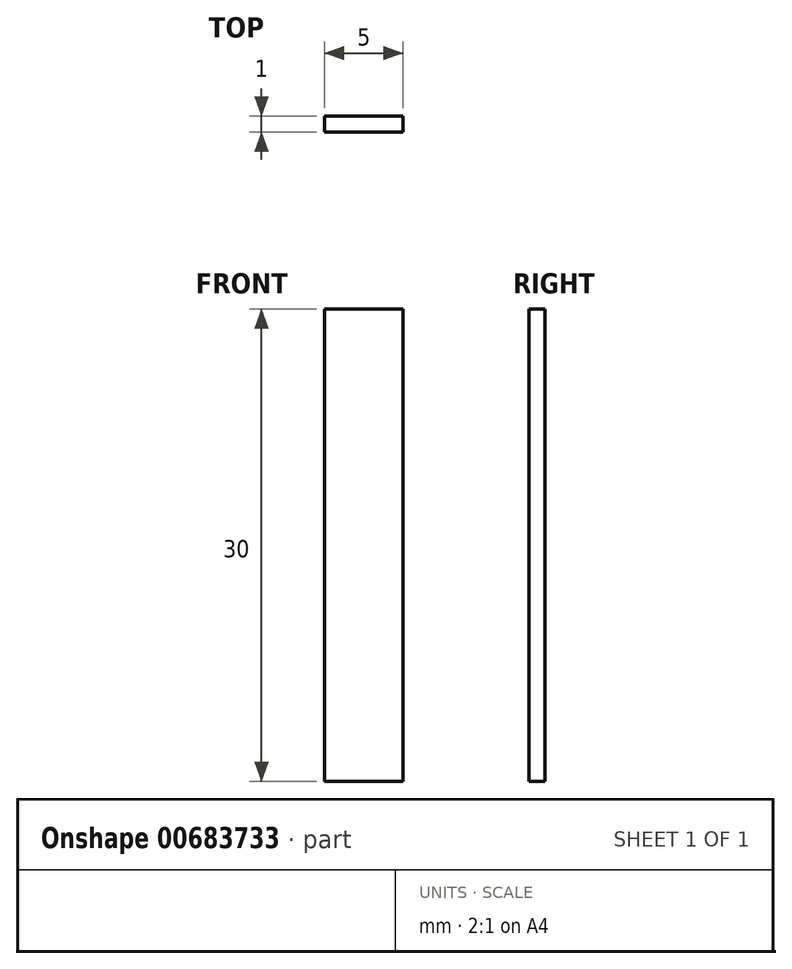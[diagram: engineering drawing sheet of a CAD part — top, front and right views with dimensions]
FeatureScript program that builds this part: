
annotation { "Feature Type Name" : "Feature", "Feature Type Description" : "" }
export const myFeature = defineFeature(function(context is Context, id is Id, definition is map)
    precondition{}
    {
        {
            var Q0;
            Q0=qCreatedBy(makeId("Front.planeOp"),FACE);
            var sketch = newSketch(context, id + "F0", { "sketchPlane" : qUnion([Q0])});
            skLineSegment(sketch, "E0.bottom", {"start": v(-40.38, 15) * mm, "end": v(-35.38, 15) * mm});
            skLineSegment(sketch, "E0.top", {"start": v(-40.38, -15) * mm, "end": v(-35.38, -15) * mm});
            skLineSegment(sketch, "E0.left", {"start": v(-40.38, 15) * mm, "end": v(-40.38, -15) * mm});
            skLineSegment(sketch, "E0.right", {"start": v(-35.38, 15) * mm, "end": v(-35.38, -15) * mm});
            skSolve(sketch);
        }
        {
            var Q0;
            Q0 = qSketchRegion(id + "F0", true);
            extrude(context, id + "F1", {"entities" : qUnion([Q0]), "depth" : 1 * mm, "offsetDistance" : 25.4 * mm});
        }
    });
